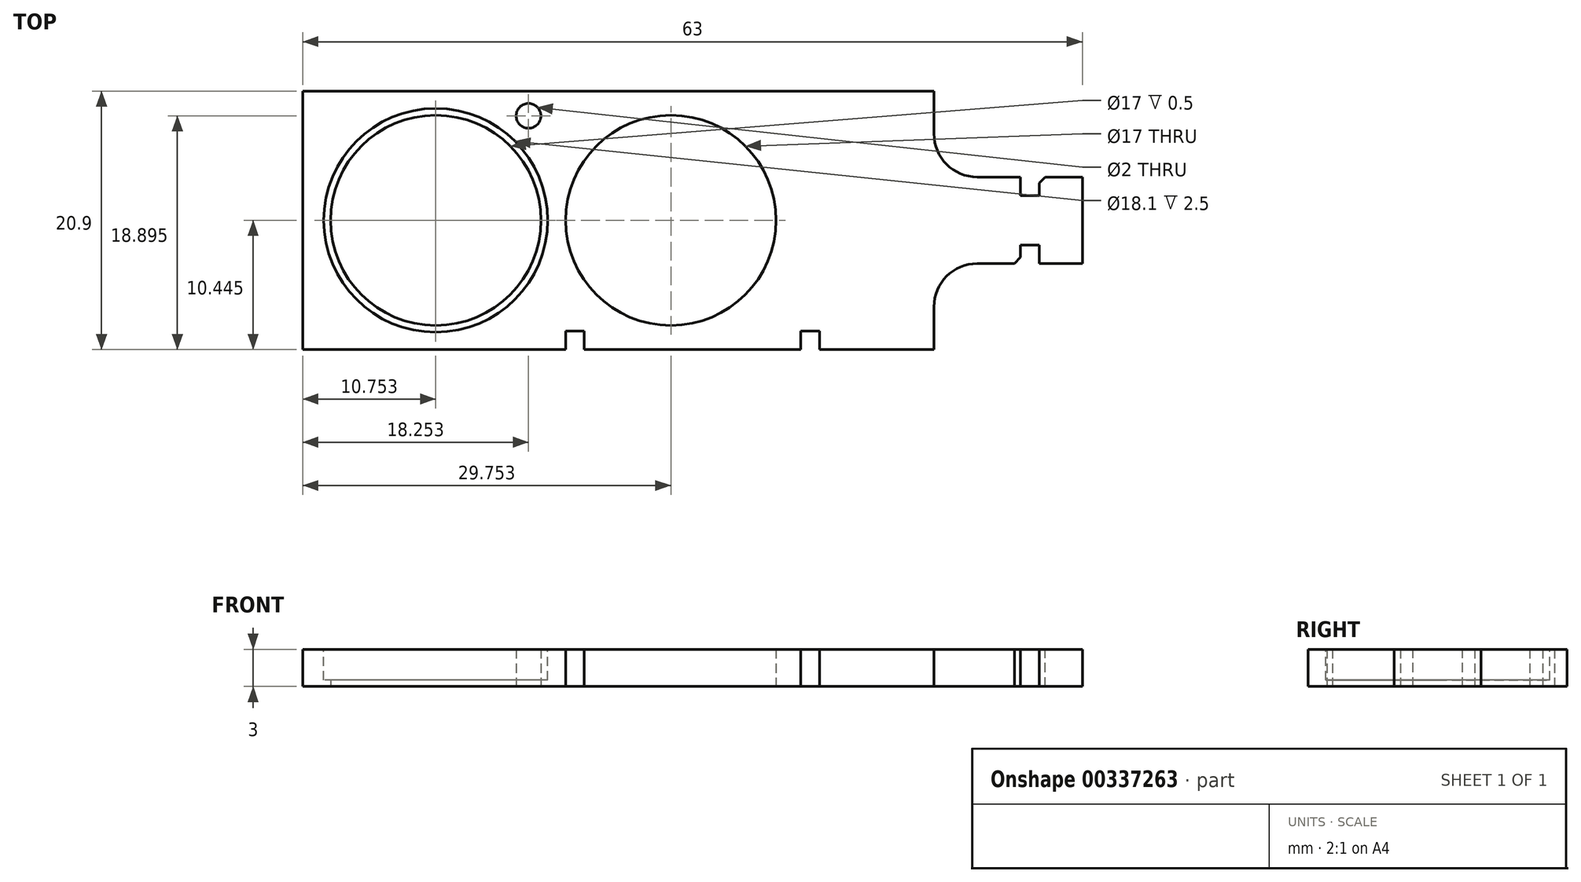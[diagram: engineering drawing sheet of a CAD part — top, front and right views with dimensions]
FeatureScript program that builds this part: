
annotation { "Feature Type Name" : "Feature", "Feature Type Description" : "" }
export const myFeature = defineFeature(function(context is Context, id is Id, definition is map)
    precondition{}
    {
        {
            var Q0;
            Q0=qCreatedBy(makeId("Top.planeOp"),FACE);
            var sketch = newSketch(context, id + "F0", { "sketchPlane" : qUnion([Q0])});
            skLineSegment(sketch, "E0", {"start": v(-30.6, 13.17) * mm, "end": v(20.4, 13.17) * mm});
            skLineSegment(sketch, "E1", {"start": v(20.4, 13.17) * mm, "end": v(20.4, 9.72) * mm});
            skLineSegment(sketch, "E2", {"start": v(23.9, 6.22) * mm, "end": v(32.4, 6.22) * mm});
            skLineSegment(sketch, "E3", {"start": v(32.4, 6.22) * mm, "end": v(32.4, -0.78) * mm});
            skLineSegment(sketch, "E4", {"start": v(32.4, -0.78) * mm, "end": v(23.9, -0.78) * mm});
            skLineSegment(sketch, "E5", {"start": v(20.4, -4.28) * mm, "end": v(20.4, -7.73) * mm});
            skLineSegment(sketch, "E6", {"start": v(-30.6, -7.73) * mm, "end": v(-30.6, 13.17) * mm});
            skPoint(sketch, "E7.orphan", {"position": v(-29.62, 13.17) * mm});
            skPoint(sketch, "E8.visualSharp", {"position": v(20.4, -0.78) * mm});
            skArc(sketch, "E8.filletArc", {"start": v(23.9, -0.78) * mm, "mid": v(21.42, -1.81) * mm, "end": v(20.4, -4.28) * mm});
            skPoint(sketch, "E9.visualSharp", {"position": v(20.4, 6.22) * mm});
            skArc(sketch, "E9.filletArc", {"start": v(20.4, 9.72) * mm, "mid": v(21.42, 7.24) * mm, "end": v(23.9, 6.22) * mm});
            skCircle(sketch, "E10", {"center": v(-19.86, 2.72) * mm, "radius": 8.5 * mm});
            skCircle(sketch, "E11", {"center": v(-0.86, 2.72) * mm, "radius": 8.5 * mm});
            skCircle(sketch, "E12", {"center": v(-12.36, 11.17) * mm, "radius": 1 * mm});
            skLineSegment(sketch, "E13.bottom", {"start": v(-9.36, -6.23) * mm, "end": v(-7.86, -6.23) * mm});
            skLineSegment(sketch, "E13.left", {"start": v(-9.36, -6.23) * mm, "end": v(-9.36, -7.73) * mm});
            skLineSegment(sketch, "E13.right", {"start": v(-7.86, -6.23) * mm, "end": v(-7.86, -7.73) * mm});
            skLineSegment(sketch, "E14.bottom", {"start": v(9.64, -6.23) * mm, "end": v(11.14, -6.23) * mm});
            skLineSegment(sketch, "E14.left", {"start": v(9.64, -6.23) * mm, "end": v(9.64, -7.73) * mm});
            skLineSegment(sketch, "E14.right", {"start": v(11.14, -6.23) * mm, "end": v(11.14, -7.73) * mm});
            skPoint(sketch, "E15", {"position": v(-8.6, -6.23) * mm});
            skPoint(sketch, "E16", {"position": v(10.4, -6.23) * mm});
            skLineSegment(sketch, "E17.trimOffspring", {"start": v(-9.36, -7.73) * mm, "end": v(-30.6, -7.73) * mm});
            skLineSegment(sketch, "E18.trimOffspring", {"start": v(9.64, -7.73) * mm, "end": v(-7.86, -7.73) * mm});
            skLineSegment(sketch, "E19", {"start": v(11.14, -7.73) * mm, "end": v(20.4, -7.73) * mm});
            skSolve(sketch);
        }
        {
            var Q0;
            Q0 = qSketchRegion(id + "F0", true);
            extrude(context, id + "F1", {"entities" : qUnion([Q0]), "depth" : 3 * mm});
        }
        {
            var Q0;
            Q0=makeQuery(id+"F1.opExtrude","CAP_FACE",FACE,{"disambiguationData":[OSD([sQuery(id+"F0.wireOp",EDGE,"E0"),sQuery(id+"F0.wireOp",EDGE,"E1"),sQuery(id+"F0.wireOp",EDGE,"E2"),sQuery(id+"F0.wireOp",EDGE,"E3"),sQuery(id+"F0.wireOp",EDGE,"E4"),sQuery(id+"F0.wireOp",EDGE,"E5"),sQuery(id+"F0.wireOp",EDGE,"E6"),sQuery(id+"F0.wireOp",EDGE,"E8.filletArc"),sQuery(id+"F0.wireOp",EDGE,"E9.filletArc"),sQuery(id+"F0.wireOp",EDGE,"E10"),sQuery(id+"F0.wireOp",EDGE,"E11"),sQuery(id+"F0.wireOp",EDGE,"E12"),sQuery(id+"F0.wireOp",EDGE,"E13.bottom"),sQuery(id+"F0.wireOp",EDGE,"E13.left"),sQuery(id+"F0.wireOp",EDGE,"E13.right"),sQuery(id+"F0.wireOp",EDGE,"E14.bottom"),sQuery(id+"F0.wireOp",EDGE,"E14.left"),sQuery(id+"F0.wireOp",EDGE,"E14.right"),sQuery(id+"F0.wireOp",EDGE,"E17.trimOffspring"),sQuery(id+"F0.wireOp",EDGE,"E18.trimOffspring"),sQuery(id+"F0.wireOp",EDGE,"E19")])],"isStart":false});
            var sketch = newSketch(context, id + "F2", { "sketchPlane" : qUnion([Q0])});
            skCircle(sketch, "E20", {"center": v(-19.86, 2.72) * mm, "radius": 9.05 * mm});
            skSolve(sketch);
        }
        {
            var Q0;
            Q0 = qSketchRegion(id + "F2", true);
            extrude(context, id + "F3", {"entities" : qUnion([Q0]), "operationType" : NewBodyOperationType.REMOVE, "oppositeDirection" : true, "depth" : 2.5 * mm});
        }
        {
            var Q0;
            Q0=makeQuery(id+"F1.opExtrude","CAP_FACE",FACE,{"disambiguationData":[OSD([sQuery(id+"F0.wireOp",EDGE,"E0"),sQuery(id+"F0.wireOp",EDGE,"E1"),sQuery(id+"F0.wireOp",EDGE,"E2"),sQuery(id+"F0.wireOp",EDGE,"E3"),sQuery(id+"F0.wireOp",EDGE,"E4"),sQuery(id+"F0.wireOp",EDGE,"E5"),sQuery(id+"F0.wireOp",EDGE,"E6"),sQuery(id+"F0.wireOp",EDGE,"E8.filletArc"),sQuery(id+"F0.wireOp",EDGE,"E9.filletArc"),sQuery(id+"F0.wireOp",EDGE,"E10"),sQuery(id+"F0.wireOp",EDGE,"E11"),sQuery(id+"F0.wireOp",EDGE,"E12"),sQuery(id+"F0.wireOp",EDGE,"E13.bottom"),sQuery(id+"F0.wireOp",EDGE,"E13.left"),sQuery(id+"F0.wireOp",EDGE,"E13.right"),sQuery(id+"F0.wireOp",EDGE,"E14.bottom"),sQuery(id+"F0.wireOp",EDGE,"E14.left"),sQuery(id+"F0.wireOp",EDGE,"E14.right"),sQuery(id+"F0.wireOp",EDGE,"E17.trimOffspring"),sQuery(id+"F0.wireOp",EDGE,"E18.trimOffspring"),sQuery(id+"F0.wireOp",EDGE,"E19")])],"isStart":false});
            var sketch = newSketch(context, id + "F4", { "sketchPlane" : qUnion([Q0])});
            skLineSegment(sketch, "E21.bottom", {"start": v(27.4, -0.78) * mm, "end": v(28.9, -0.78) * mm});
            skLineSegment(sketch, "E21.top", {"start": v(27.4, 0.72) * mm, "end": v(28.9, 0.72) * mm});
            skLineSegment(sketch, "E21.left", {"start": v(27.4, -0.78) * mm, "end": v(27.4, 0.72) * mm});
            skLineSegment(sketch, "E21.right", {"start": v(28.9, -0.78) * mm, "end": v(28.9, 0.72) * mm});
            skPoint(sketch, "E22", {"position": v(28.14, -0.78) * mm});
            skLineSegment(sketch, "E23.bottom", {"start": v(28.9, 6.22) * mm, "end": v(27.4, 6.22) * mm});
            skLineSegment(sketch, "E23.top", {"start": v(28.9, 4.72) * mm, "end": v(27.4, 4.72) * mm});
            skLineSegment(sketch, "E23.left", {"start": v(28.9, 6.22) * mm, "end": v(28.9, 4.72) * mm});
            skLineSegment(sketch, "E23.right", {"start": v(27.4, 6.22) * mm, "end": v(27.4, 4.72) * mm});
            skPoint(sketch, "E24", {"position": v(28.14, 6.22) * mm});
            skSolve(sketch);
        }
        {
            var Q0;
            Q0 = qSketchRegion(id + "F4", true);
            extrude(context, id + "F5", {"entities" : qUnion([Q0]), "operationType" : NewBodyOperationType.REMOVE, "oppositeDirection" : true, "depth" : 3 * mm});
        }
        {
            var Q0;
            Q0=makeQuery(id+"F5.boolean.opBoolean","COPY",EDGE,{"derivedFrom":makeQuery(id+"F5.opExtrude","SWEPT_EDGE",EDGE,{"disambiguationData":[OSD([sQuery(id+"F0.wireOp",EDGE,"E4"),sQuery(id+"F4.wireOp",EDGE,"E21.bottom"),sQuery(id+"F4.wireOp",EDGE,"E21.left")])]})});
            var Q1;
            Q1=makeQuery(id+"F5.boolean.opBoolean","COPY",EDGE,{"derivedFrom":makeQuery(id+"F5.opExtrude","SWEPT_EDGE",EDGE,{"disambiguationData":[OSD([sQuery(id+"F0.wireOp",EDGE,"E4"),sQuery(id+"F4.wireOp",EDGE,"E21.bottom"),sQuery(id+"F4.wireOp",EDGE,"E21.right")])]})});
            var Q2;
            Q2=makeQuery(id+"F5.boolean.opBoolean","COPY",EDGE,{"derivedFrom":makeQuery(id+"F5.opExtrude","SWEPT_EDGE",EDGE,{"disambiguationData":[OSD([sQuery(id+"F0.wireOp",EDGE,"E2"),sQuery(id+"F4.wireOp",EDGE,"E23.bottom"),sQuery(id+"F4.wireOp",EDGE,"E23.left")])]})});
            var Q3;
            Q3=makeQuery(id+"F5.boolean.opBoolean","COPY",EDGE,{"derivedFrom":makeQuery(id+"F5.opExtrude","SWEPT_EDGE",EDGE,{"disambiguationData":[OSD([sQuery(id+"F0.wireOp",EDGE,"E2"),sQuery(id+"F4.wireOp",EDGE,"E23.bottom"),sQuery(id+"F4.wireOp",EDGE,"E23.right")])]})});
            chamfer(context, id + "F6", {"entities" : qUnion([Q0, Q1, Q2, Q3]), "width" : 0.5 * mm, "tangentPropagation" : true});
        }
    });
